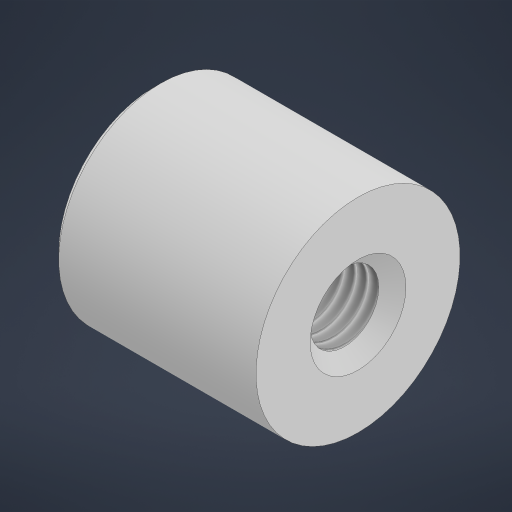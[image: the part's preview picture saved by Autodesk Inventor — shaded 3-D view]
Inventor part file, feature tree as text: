
AUTODESK INVENTOR PART (.ipt)
format: ipt  version: 2024.1 (Build 281209000, 209)  size: 186,880 bytes
history: native  units: mm
features: sketch x2, revolve x1, hole x1, chamfer x1
ambient origin geometry x8: Origin, YZ Plane, XZ Plane, XY Plane, X Axis, Y Axis, Z Axis, Center Point
bodies: Solid1 (feature_tree)
feature tree (5):
  revolve  "Revolution1"  [1 undecoded]
  hole  "Hole1"  [1 undecoded]
  chamfer  "Chamfer1"  [1 undecoded]
  sketch  "Sketch1"  dims[d0=30.0mm d1=30.0mm]
  sketch  "Sketch2"  dims[d2=90.0deg d3=10.106mm d4=10.0mm d5=14.1mm d6=2.0mm d7=90.0deg d8=15.0mm d9=20.594885mm d10=1.0mm d11=2.0mm d12=45.0deg]
note: 3 required parameter values undecoded (feature->parameter linkage not recoverable at this tier; creation-order binding heuristic only, values carry confidence <= 0.55)